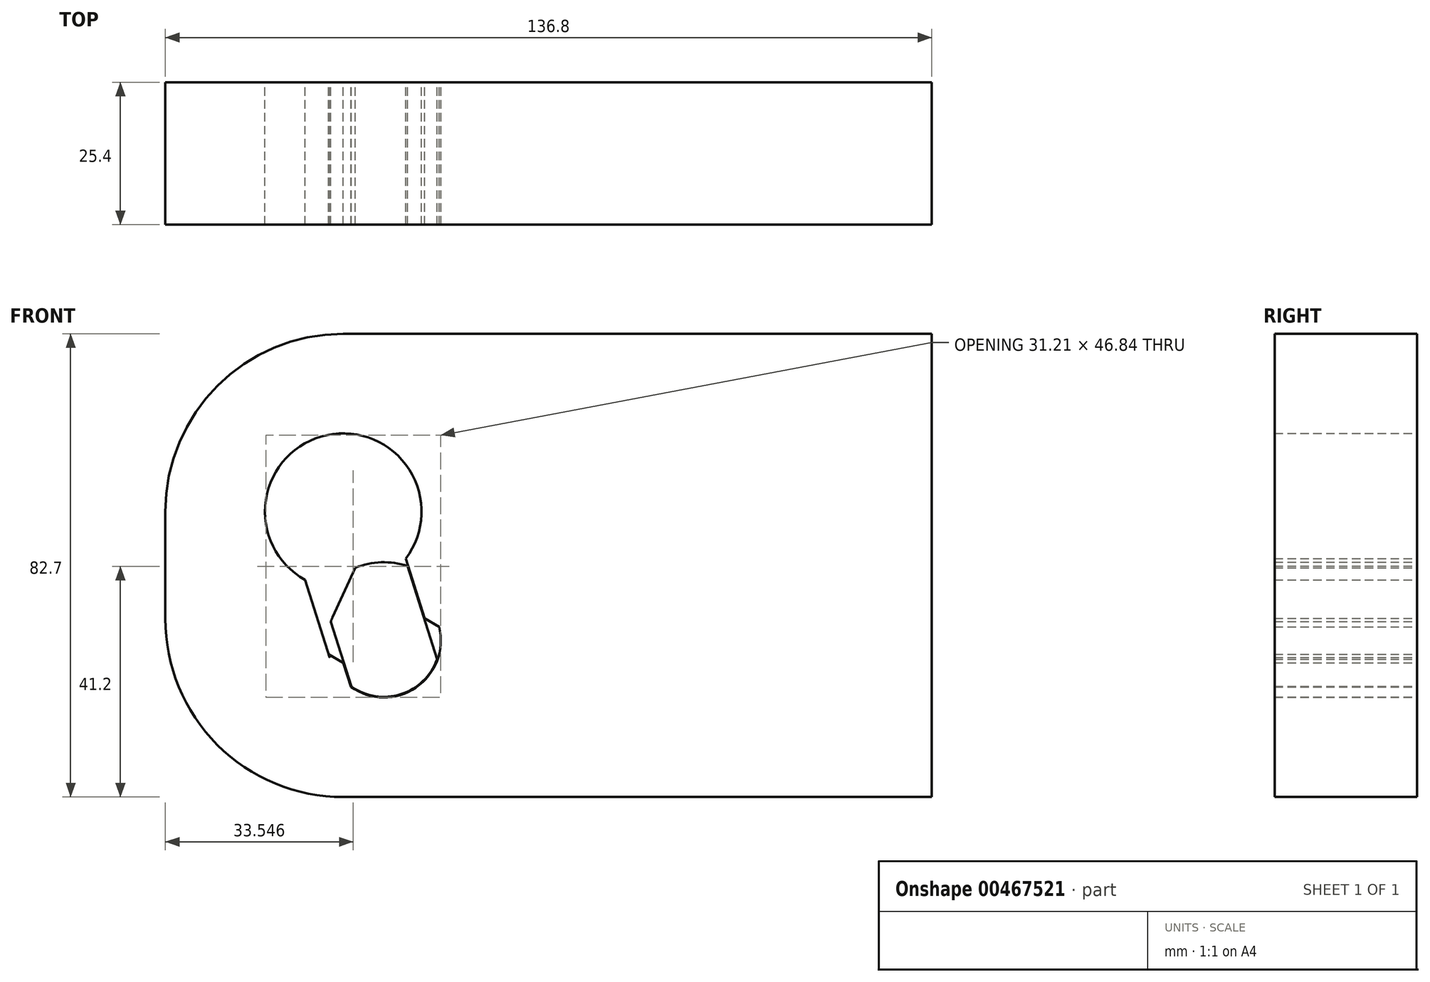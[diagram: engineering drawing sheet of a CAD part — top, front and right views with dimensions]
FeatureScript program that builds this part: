
annotation { "Feature Type Name" : "Feature", "Feature Type Description" : "" }
export const myFeature = defineFeature(function(context is Context, id is Id, definition is map)
    precondition{}
    {
        {
            var Q0;
            Q0=qCreatedBy(makeId("Front.planeOp"),FACE);
            var sketch = newSketch(context, id + "F0", { "sketchPlane" : qUnion([Q0])});
            skCircle(sketch, "E0", {"center": v(0, 0) * mm, "radius": 10.16 * mm});
            skLineSegment(sketch, "E1", {"start": v(0, 0) * mm, "end": v(0, 63.5) * mm, "construction": true});
            skLineSegment(sketch, "E2", {"start": v(0, 0) * mm, "end": v(-19.1, 60.56) * mm, "construction": true});
            skLineSegment(sketch, "E3", {"start": v(0, 0) * mm, "end": v(-7.26, 23.01) * mm, "construction": true});
            skCircle(sketch, "E4", {"center": v(-7.26, 23.01) * mm, "radius": 13.97 * mm});
            skLineSegment(sketch, "E5", {"start": v(0, 0) * mm, "end": v(-9.69, -3.06) * mm, "construction": true});
            skLineSegment(sketch, "E6", {"start": v(-9.69, -3.06) * mm, "end": v(-14.06, 10.81) * mm});
            skLineSegment(sketch, "E7", {"start": v(0, 0) * mm, "end": v(9.69, 3.06) * mm, "construction": true});
            skLineSegment(sketch, "E8", {"start": v(9.69, 3.06) * mm, "end": v(-4.9, 49.33) * mm, "construction": true});
            skLineSegment(sketch, "E9", {"start": v(9.69, 3.06) * mm, "end": v(7.75, 2.44) * mm, "construction": true});
            skLineSegment(sketch, "E10", {"start": v(7.75, 2.44) * mm, "end": v(3.91, 14.62) * mm, "construction": true});
            skLineSegment(sketch, "E11", {"start": v(3.91, 14.62) * mm, "end": v(5.92, 8.26) * mm});
            skLineSegment(sketch, "E12", {"start": v(0, -10.16) * mm, "end": v(0, -27.94) * mm, "construction": true});
            skLineSegment(sketch, "E13", {"start": v(-7.26, 23.01) * mm, "end": v(-21.23, 23.01) * mm, "construction": true});
            skLineSegment(sketch, "E14", {"start": v(-21.23, 23.01) * mm, "end": v(-39, 23.01) * mm, "construction": true});
            skLineSegment(sketch, "E15", {"start": v(-7.26, 36.98) * mm, "end": v(-7.26, 54.76) * mm, "construction": true});
            skArc(sketch, "E16", {"start": v(-7.26, 54.76) * mm, "mid": v(-29.7, 45.46) * mm, "end": v(-39, 23.01) * mm});
            skLineSegment(sketch, "E17", {"start": v(0, -27.94) * mm, "end": v(-7.26, -27.94) * mm, "construction": true});
            skLineSegment(sketch, "E18", {"start": v(-7.26, -27.94) * mm, "end": v(-7.26, 3.8) * mm, "construction": true});
            skArc(sketch, "E19", {"start": v(-39, 3.88) * mm, "mid": v(-29.73, -18.62) * mm, "end": v(-7.26, -27.94) * mm});
            skPoint(sketch, "E19.startSnap0", {"position": v(-11.88, 3.88) * mm});
            skLineSegment(sketch, "E20", {"start": v(-39, 23.01) * mm, "end": v(-39, 3.88) * mm});
            skLineSegment(sketch, "E21", {"start": v(-7.26, 54.76) * mm, "end": v(0, 54.76) * mm});
            skLineSegment(sketch, "E22", {"start": v(-7.26, -27.94) * mm, "end": v(0, -27.94) * mm});
            skLineSegment(sketch, "E23", {"start": v(0, 54.76) * mm, "end": v(97.8, 54.76) * mm});
            skLineSegment(sketch, "E24", {"start": v(97.8, 54.76) * mm, "end": v(97.8, -27.94) * mm});
            skLineSegment(sketch, "E25", {"start": v(97.8, -27.94) * mm, "end": v(0, -27.94) * mm});
            skLineSegment(sketch, "E26", {"start": v(0, 0) * mm, "end": v(5.16, 8.75) * mm, "construction": true});
            skLineSegment(sketch, "E27", {"start": v(5.16, 8.75) * mm, "end": v(3.6, 6.13) * mm, "construction": true});
            skLineSegment(sketch, "E28", {"start": v(3.6, 6.13) * mm, "end": v(9.86, 2.45) * mm, "construction": true});
            skLineSegment(sketch, "E29", {"start": v(9.86, 2.45) * mm, "end": v(7.27, 3.97) * mm});
            skLineSegment(sketch, "E30", {"start": v(7.27, 3.97) * mm, "end": v(5.92, 8.26) * mm});
            skLineSegment(sketch, "E31", {"start": v(-9.69, -3.06) * mm, "end": v(-7.75, -2.44) * mm, "construction": true});
            skLineSegment(sketch, "E32", {"start": v(-7.75, -2.44) * mm, "end": v(-11.6, 9.73) * mm, "construction": true});
            skLineSegment(sketch, "E33", {"start": v(-11.6, 9.73) * mm, "end": v(-9.58, 3.37) * mm});
            skLineSegment(sketch, "E34", {"start": v(0, 0) * mm, "end": v(-5.16, -8.75) * mm, "construction": true});
            skLineSegment(sketch, "E35", {"start": v(-5.16, -8.75) * mm, "end": v(-3.6, -6.13) * mm, "construction": true});
            skLineSegment(sketch, "E36", {"start": v(-3.6, -6.13) * mm, "end": v(-9.86, -2.45) * mm, "construction": true});
            skLineSegment(sketch, "E37", {"start": v(-9.86, -2.45) * mm, "end": v(-7.26, -3.98) * mm});
            skLineSegment(sketch, "E38", {"start": v(-7.26, -3.98) * mm, "end": v(-7.26, -7.11) * mm});
            skLineSegment(sketch, "E39", {"start": v(-7.26, -3.98) * mm, "end": v(-5.9, -8.27) * mm});
            skSolve(sketch);
        }
        {
            var Q0;
            Q0=qCreatedBy(makeId("Front.planeOp"),FACE);
            var sketch = newSketch(context, id + "F1", { "sketchPlane" : qUnion([Q0])});
            skCircle(sketch, "E40", {"center": v(0, 0) * mm, "radius": 10.06 * mm});
            skLineSegment(sketch, "E41", {"start": v(0, 0) * mm, "end": v(9.6, 3.02) * mm, "construction": true});
            skLineSegment(sketch, "E42", {"start": v(9.6, 3.02) * mm, "end": v(7.65, 2.41) * mm, "construction": true});
            skLineSegment(sketch, "E43", {"start": v(7.65, 2.41) * mm, "end": v(5.83, 8.2) * mm, "construction": true});
            skLineSegment(sketch, "E44", {"start": v(5.83, 8.2) * mm, "end": v(9.48, -3.37) * mm});
            skCircle(sketch, "E45", {"center": v(0, 0) * mm, "radius": 13.97 * mm, "construction": true});
            skLineSegment(sketch, "E46", {"start": v(5.83, 8.2) * mm, "end": v(4.22, 13.32) * mm});
            skLineSegment(sketch, "E47", {"start": v(0, 0) * mm, "end": v(-9.15, 4.17) * mm, "construction": true});
            skLineSegment(sketch, "E48", {"start": v(-9.15, 4.17) * mm, "end": v(-5.13, 13) * mm, "construction": true});
            skLineSegment(sketch, "E49", {"start": v(-9.15, 4.17) * mm, "end": v(-5.13, 13) * mm});
            skArc(sketch, "E50", {"start": v(4.22, 13.32) * mm, "mid": v(-0.49, 13.96) * mm, "end": v(-5.13, 13) * mm});
            skLineSegment(sketch, "E51", {"start": v(0, 0) * mm, "end": v(-9.6, -3.02) * mm, "construction": true});
            skLineSegment(sketch, "E52", {"start": v(-9.6, -3.02) * mm, "end": v(-7.65, -2.41) * mm, "construction": true});
            skLineSegment(sketch, "E53", {"start": v(-7.65, -2.41) * mm, "end": v(-9.48, 3.37) * mm, "construction": true});
            skLineSegment(sketch, "E54", {"start": v(-9.48, 3.37) * mm, "end": v(-5.83, -8.2) * mm});
            skSolve(sketch);
        }
        {
            var Q0;
            {var subQ0=sQuery(id+"F1.wireOp",EDGE,"E44");Q0=makeQuery(id+"F1.imprint","IMPRINT",FACE,{"disambiguationData":[TD([[makeQuery(id+"F1.imprint","IMPRINT",EDGE,{"derivedFrom":subQ0}),-1.0]])]});}
            var Q1;
            {var subQ0=sQuery(id+"F1.wireOp",EDGE,"E46");Q1=makeQuery(id+"F1.imprint","IMPRINT",FACE,{"disambiguationData":[TD([[makeQuery(id+"F1.imprint","IMPRINT",EDGE,{"derivedFrom":subQ0}),1.0]])]});}
            extrude(context, id + "F2", {"entities" : qUnion([Q0, Q1]), "depth" : 25.4 * mm});
        }
        {
            var Q0;
            {var subQ1=sQuery(id+"F0.wireOp",EDGE,"E6");Q0=makeQuery(id+"F0.imprint","IMPRINT",FACE,{"disambiguationData":[TD([[makeQuery(id+"F0.imprint","IMPRINT",EDGE,{"derivedFrom":subQ1}),1.0]])]});}
            var Q1;
            {var subQ0=sQuery(id+"F0.wireOp",EDGE,"E38");Q1=makeQuery(id+"F0.imprint","IMPRINT",FACE,{"disambiguationData":[TD([[makeQuery(id+"F0.imprint","IMPRINT",EDGE,{"derivedFrom":subQ0}),1.0]])]});}
            var Q2;
            {var subQ2=sQuery(id+"F0.wireOp",EDGE,"E37");Q2=makeQuery(id+"F0.imprint","IMPRINT",FACE,{"disambiguationData":[TD([[makeQuery(id+"F0.imprint","IMPRINT",EDGE,{"derivedFrom":subQ2}),-1.0]])]});}
            var Q3;
            {var subQ2=sQuery(id+"F0.wireOp",EDGE,"E29");Q3=makeQuery(id+"F0.imprint","IMPRINT",FACE,{"disambiguationData":[TD([[makeQuery(id+"F0.imprint","IMPRINT",EDGE,{"derivedFrom":subQ2}),-1.0]])]});}
            extrude(context, id + "F3", {"entities" : qUnion([Q0, Q1, Q2, Q3]), "depth" : 25.4 * mm});
        }
    });
